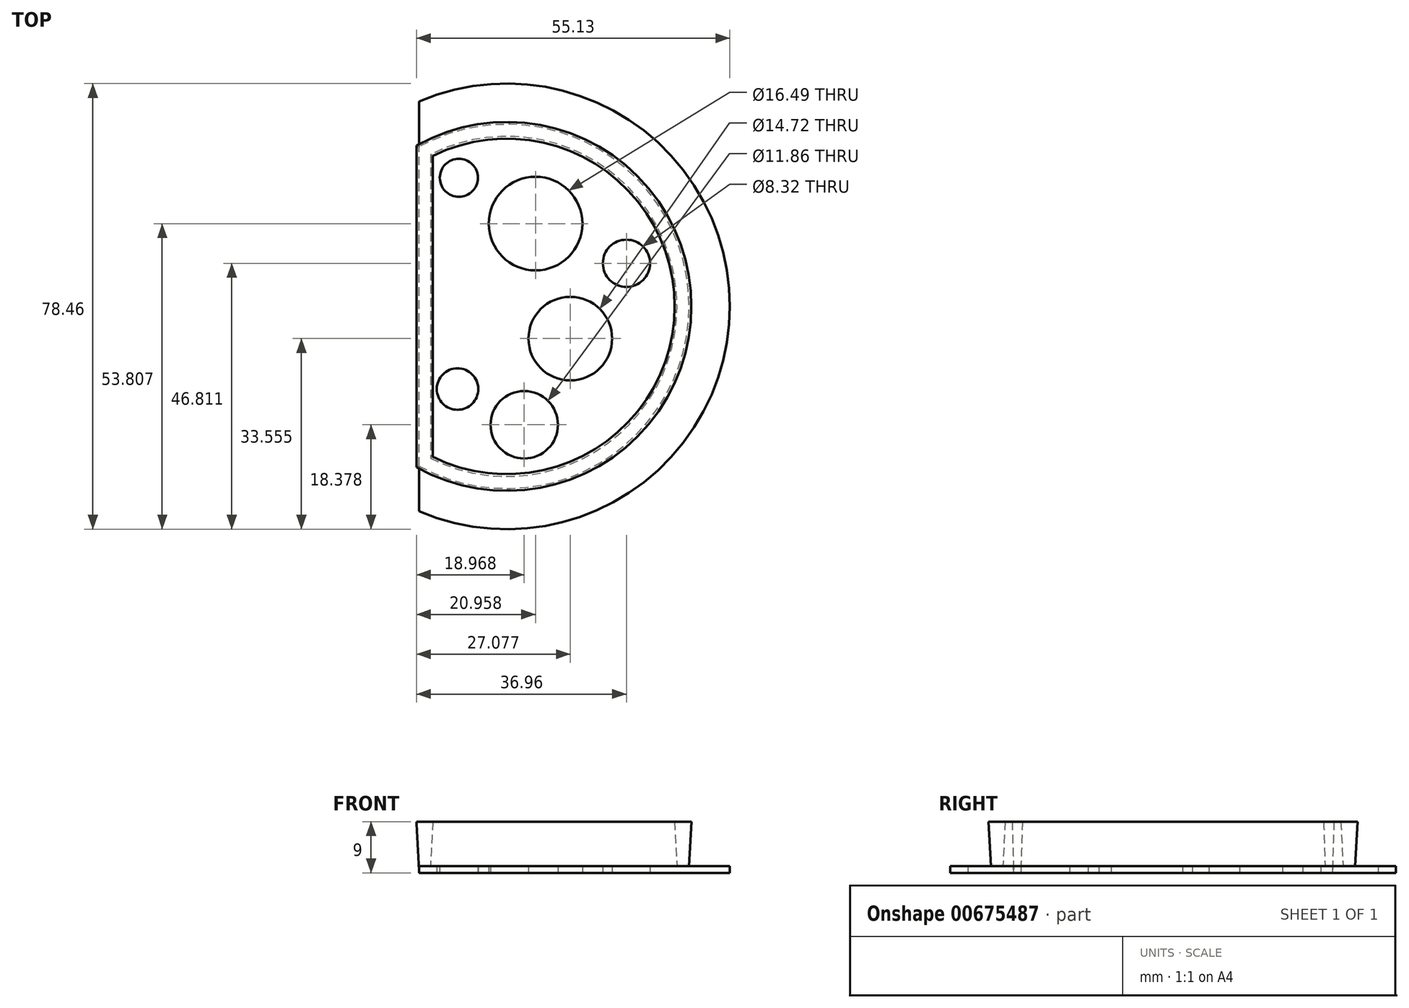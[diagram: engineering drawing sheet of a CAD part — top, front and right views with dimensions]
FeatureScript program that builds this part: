
annotation { "Feature Type Name" : "Feature", "Feature Type Description" : "" }
export const myFeature = defineFeature(function(context is Context, id is Id, definition is map)
    precondition{}
    {
        {
            var Q0;
            Q0=qCreatedBy(makeId("Top.planeOp"),FACE);
            var sketch = newSketch(context, id + "F0", { "sketchPlane" : qUnion([Q0])});
            skArc(sketch, "E0", {"start": v(-15.43, -28.03) * mm, "mid": v(32, 0) * mm, "end": v(-15.43, 28.03) * mm});
            skArc(sketch, "E1", {"start": v(-13.49, -26.8) * mm, "mid": v(30, 0) * mm, "end": v(-13.49, 26.8) * mm});
            skArc(sketch, "E2", {"start": v(-15.43, -36.07) * mm, "mid": v(39.23, 0) * mm, "end": v(-15.43, 36.07) * mm});
            skLineSegment(sketch, "E3", {"start": v(-15.43, 36.07) * mm, "end": v(-15.43, -36.07) * mm});
            skLineSegment(sketch, "E4", {"start": v(-13.49, 26.8) * mm, "end": v(-13.49, -26.8) * mm});
            skCircle(sketch, "E5", {"center": v(-8.44, 22.65) * mm, "radius": 3.35 * mm});
            skCircle(sketch, "E6", {"center": v(5.06, 14.58) * mm, "radius": 8.25 * mm});
            skCircle(sketch, "E7", {"center": v(11.18, -5.67) * mm, "radius": 7.36 * mm});
            skCircle(sketch, "E8", {"center": v(-8.67, -14.56) * mm, "radius": 3.65 * mm});
            skCircle(sketch, "E9", {"center": v(3.07, -20.85) * mm, "radius": 5.93 * mm});
            skCircle(sketch, "E10", {"center": v(21.06, 7.58) * mm, "radius": 4.16 * mm});
            skSolve(sketch);
        }
        {
            var Q0;
            {var subQ0=sQuery(id+"F0.wireOp",EDGE,"E0");Q0=makeQuery(id+"F0.imprint","IMPRINT",FACE,{"disambiguationData":[TD([[makeQuery(id+"F0.imprint","IMPRINT",EDGE,{"derivedFrom":subQ0}),-1.0]])]});}
            extrude(context, id + "F1", {"entities" : qUnion([Q0]), "depth" : 1.2 * mm, "offsetDistance" : 25 * mm});
        }
        {
            var Q0;
            {var subQ0=sQuery(id+"F0.wireOp",EDGE,"E0");Q0=makeQuery(id+"F0.imprint","IMPRINT",FACE,{"disambiguationData":[TD([[makeQuery(id+"F0.imprint","IMPRINT",EDGE,{"derivedFrom":subQ0}),1.0]])]});}
            extrude(context, id + "F2", {"entities" : qUnion([Q0]), "operationType" : NewBodyOperationType.ADD, "depth" : 9 * mm, "offsetDistance" : 25 * mm, "hasDraft" : true, "draftAngle" : 3 * degree});
        }
        {
            var Q0;
            Q0=makeQuery(id+"F0.imprint","IMPRINT",FACE,{"disambiguationData":[TD([[makeQuery(id+"F0.imprint","IMPRINT",EDGE,{"derivedFrom":sQuery(id+"F0.wireOp",EDGE,"E1")}),1.0]])]});
            extrude(context, id + "F3", {"entities" : qUnion([Q0]), "operationType" : NewBodyOperationType.ADD, "depth" : 1.2 * mm, "offsetDistance" : 25 * mm});
        }
    });
